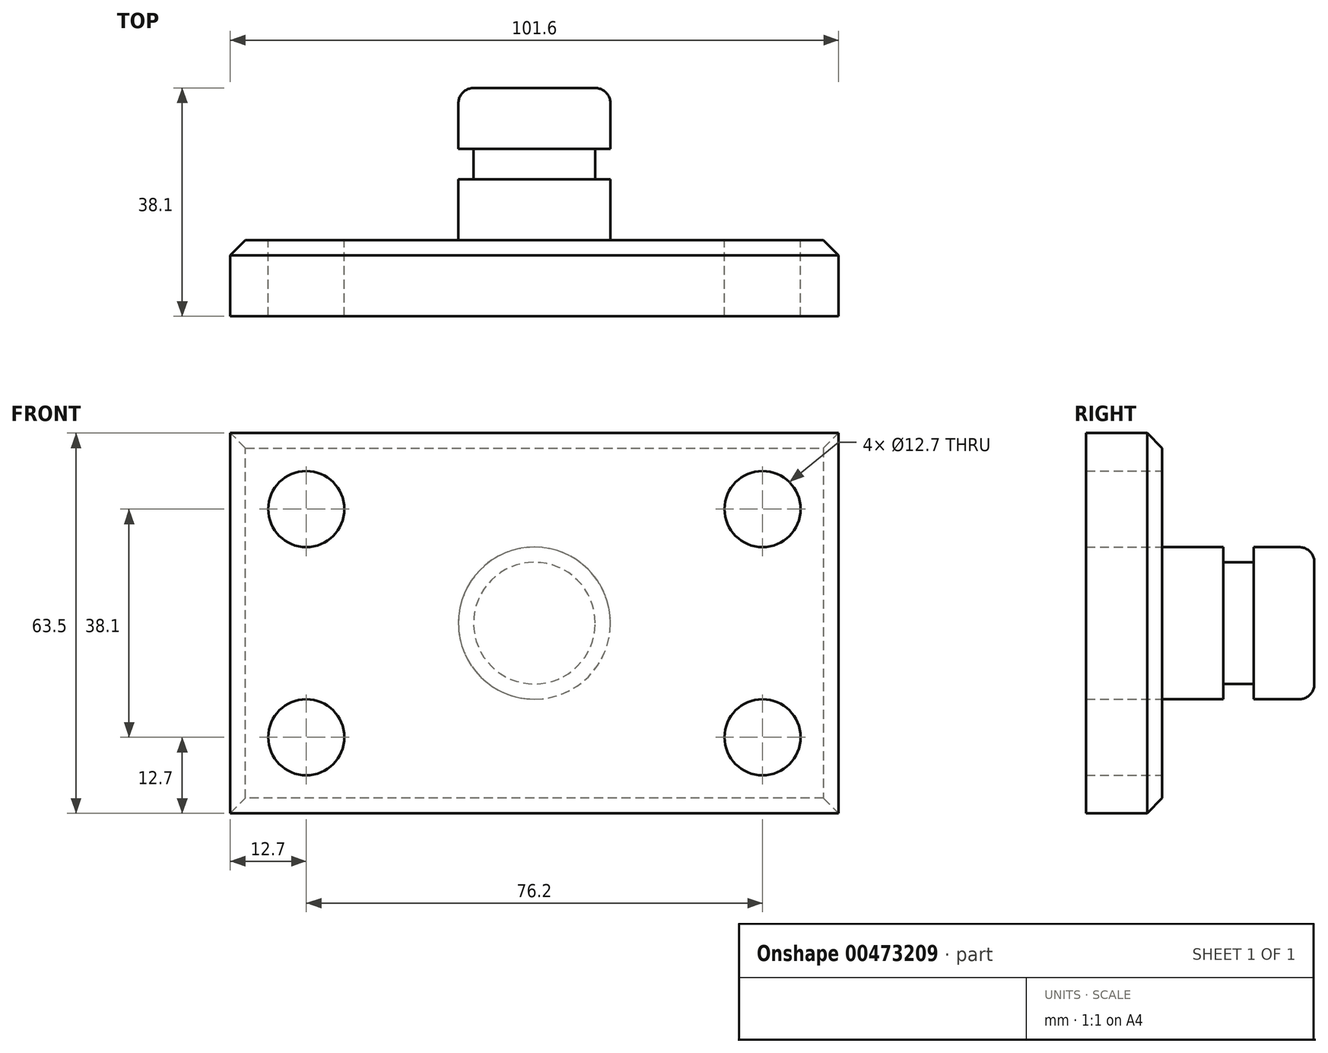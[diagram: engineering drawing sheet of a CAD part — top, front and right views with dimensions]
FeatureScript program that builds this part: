
annotation { "Feature Type Name" : "Feature", "Feature Type Description" : "" }
export const myFeature = defineFeature(function(context is Context, id is Id, definition is map)
    precondition{}
    {
        {
            var Q0;
            Q0=qCreatedBy(makeId("Front.planeOp"),FACE);
            var sketch = newSketch(context, id + "F0", { "sketchPlane" : qUnion([Q0])});
            skLineSegment(sketch, "E0.bottom", {"start": v(-50.8, -31.75) * mm, "end": v(50.8, -31.75) * mm});
            skLineSegment(sketch, "E0.top", {"start": v(-50.8, 31.75) * mm, "end": v(50.8, 31.75) * mm});
            skLineSegment(sketch, "E0.left", {"start": v(-50.8, -31.75) * mm, "end": v(-50.8, 31.75) * mm});
            skLineSegment(sketch, "E0.right", {"start": v(50.8, -31.75) * mm, "end": v(50.8, 31.75) * mm});
            skPoint(sketch, "E0.middle", {"position": v(0, 0) * mm});
            skSolve(sketch);
        }
        {
            var Q0;
            Q0=makeQuery(id+"F0.imprint","IMPRINT",FACE,{"disambiguationData":[TD([[makeQuery(id+"F0.imprint","IMPRINT",EDGE,{"derivedFrom":sQuery(id+"F0.wireOp",EDGE,"E0.bottom")}),1.0]])]});
            extrude(context, id + "F1", {"entities" : qUnion([Q0]), "oppositeDirection" : true, "depth" : 12.7 * mm});
        }
        {
            var Q0;
            Q0=makeQuery(id+"F1.opExtrude","CAP_FACE",FACE,{"disambiguationData":[OSD([sQuery(id+"F0.wireOp",EDGE,"E0.bottom"),sQuery(id+"F0.wireOp",EDGE,"E0.top"),sQuery(id+"F0.wireOp",EDGE,"E0.left"),sQuery(id+"F0.wireOp",EDGE,"E0.right")])],"isStart":false});
            var sketch = newSketch(context, id + "F2", { "sketchPlane" : qUnion([Q0])});
            skCircle(sketch, "E1", {"center": v(38.1, -19.05) * mm, "radius": 6.35 * mm});
            skCircle(sketch, "E2", {"center": v(-38.1, -19.05) * mm, "radius": 6.35 * mm});
            skCircle(sketch, "E3", {"center": v(38.1, 19.05) * mm, "radius": 6.35 * mm});
            skCircle(sketch, "E4", {"center": v(-38.1, 19.05) * mm, "radius": 6.35 * mm});
            skSolve(sketch);
        }
        {
            var Q0;
            Q0 = qSketchRegion(id + "F2", true);
            extrude(context, id + "F3", {"entities" : qUnion([Q0]), "operationType" : NewBodyOperationType.REMOVE, "endBound" : BoundingType.THROUGH_ALL, "oppositeDirection" : true, "depth" : 25.4 * mm});
        }
        {
            var Q0;
            Q0=qCreatedBy(makeId("Top.planeOp"),FACE);
            var sketch = newSketch(context, id + "F4", { "sketchPlane" : qUnion([Q0])});
            skLineSegment(sketch, "E5.bottom", {"start": v(0, 0) * mm, "end": v(0, 0) * mm});
            skLineSegment(sketch, "E5.top", {"start": v(0, 12.7) * mm, "end": v(0, 12.7) * mm});
            skLineSegment(sketch, "E5.left", {"start": v(0, 0) * mm, "end": v(0, 12.7) * mm});
            skLineSegment(sketch, "E5.right", {"start": v(0, 0) * mm, "end": v(0, 12.7) * mm});
            skLineSegment(sketch, "E6.bottom", {"start": v(0, 12.7) * mm, "end": v(12.7, 12.7) * mm});
            skLineSegment(sketch, "E6.top", {"start": v(0, 38.1) * mm, "end": v(12.7, 38.1) * mm});
            skLineSegment(sketch, "E6.left", {"start": v(0, 12.7) * mm, "end": v(0, 38.1) * mm});
            skLineSegment(sketch, "E6.right", {"start": v(12.7, 12.7) * mm, "end": v(12.7, 38.1) * mm});
            skSolve(sketch);
        }
        {
            var Q0;
            Q0=makeQuery(id+"F4.imprint","IMPRINT",FACE,{"disambiguationData":[TD([[makeQuery(id+"F4.imprint","IMPRINT",EDGE,{"derivedFrom":sQuery(id+"F4.wireOp",EDGE,"E6.bottom")}),1.0]])]});
            var Q1;
            Q1=sQuery(id+"F4.wireOp",EDGE,"E6.left");
            revolve(context, id + "F5", {"operationType" : NewBodyOperationType.ADD, "entities" : qUnion([Q0]), "axis" : qUnion([Q1]), "revolveType" : RevolveType.FULL});
        }
        {
            var Q0;
            Q0=qCreatedBy(makeId("Top.planeOp"),FACE);
            var sketch = newSketch(context, id + "F6", { "sketchPlane" : qUnion([Q0])});
            skLineSegment(sketch, "E7.bottom", {"start": v(-19.23, 22.86) * mm, "end": v(-10.16, 22.86) * mm});
            skLineSegment(sketch, "E7.top", {"start": v(-19.23, 27.94) * mm, "end": v(-10.16, 27.94) * mm});
            skLineSegment(sketch, "E7.left", {"start": v(-19.23, 22.86) * mm, "end": v(-19.23, 27.94) * mm});
            skLineSegment(sketch, "E7.right", {"start": v(-10.16, 22.86) * mm, "end": v(-10.16, 27.94) * mm});
            skSolve(sketch);
        }
        {
            var Q0;
            Q0=makeQuery(id+"F6.imprint","IMPRINT",FACE,{"disambiguationData":[TD([[makeQuery(id+"F6.imprint","IMPRINT",EDGE,{"derivedFrom":sQuery(id+"F6.wireOp",EDGE,"E7.bottom")}),1.0]])]});
            var Q1;
            Q1=makeQuery(id+"F5.opRevolve","SWEPT_FACE",FACE,{"disambiguationData":[OSD([sQuery(id+"F4.wireOp",EDGE,"E6.right")])]});
            revolve(context, id + "F7", {"operationType" : NewBodyOperationType.REMOVE, "entities" : qUnion([Q0]), "axis" : qUnion([Q1]), "revolveType" : RevolveType.FULL, "oppositeDirection" : true});
        }
        {
            var Q0;
            Q0=makeQuery(id+"F5.opRevolve","SWEPT_EDGE",EDGE,{"disambiguationData":[OSD([sQuery(id+"F4.wireOp",EDGE,"E6.bottom"),sQuery(id+"F4.wireOp",EDGE,"E6.right")])]});
            var Q1;
            Q1=makeQuery(id+"F5.opRevolve","SWEPT_FACE",FACE,{"disambiguationData":[OSD([sQuery(id+"F4.wireOp",EDGE,"E6.top")])]});
            fillet(context, id + "F8", {"entities" : qUnion([Q0, Q1]), "radius" : 2.54 * mm, "tangentPropagation" : true, "allowEdgeOverflow" : false});
        }
        {
            var Q0;
            Q0=makeQuery(id+"F1.opExtrude","CAP_EDGE",EDGE,{"disambiguationData":[OSD([sQuery(id+"F0.wireOp",EDGE,"E0.bottom")])],"isStart":false});
            var Q1;
            Q1=makeQuery(id+"F1.opExtrude","CAP_EDGE",EDGE,{"disambiguationData":[OSD([sQuery(id+"F0.wireOp",EDGE,"E0.right")])],"isStart":false});
            var Q2;
            Q2=makeQuery(id+"F1.opExtrude","CAP_EDGE",EDGE,{"disambiguationData":[OSD([sQuery(id+"F0.wireOp",EDGE,"E0.top")])],"isStart":false});
            var Q3;
            Q3=makeQuery(id+"F1.opExtrude","CAP_EDGE",EDGE,{"disambiguationData":[OSD([sQuery(id+"F0.wireOp",EDGE,"E0.left")])],"isStart":false});
            chamfer(context, id + "F9", {"entities" : qUnion([Q0, Q1, Q2, Q3]), "width" : 2.54 * mm, "tangentPropagation" : true});
        }
    });
